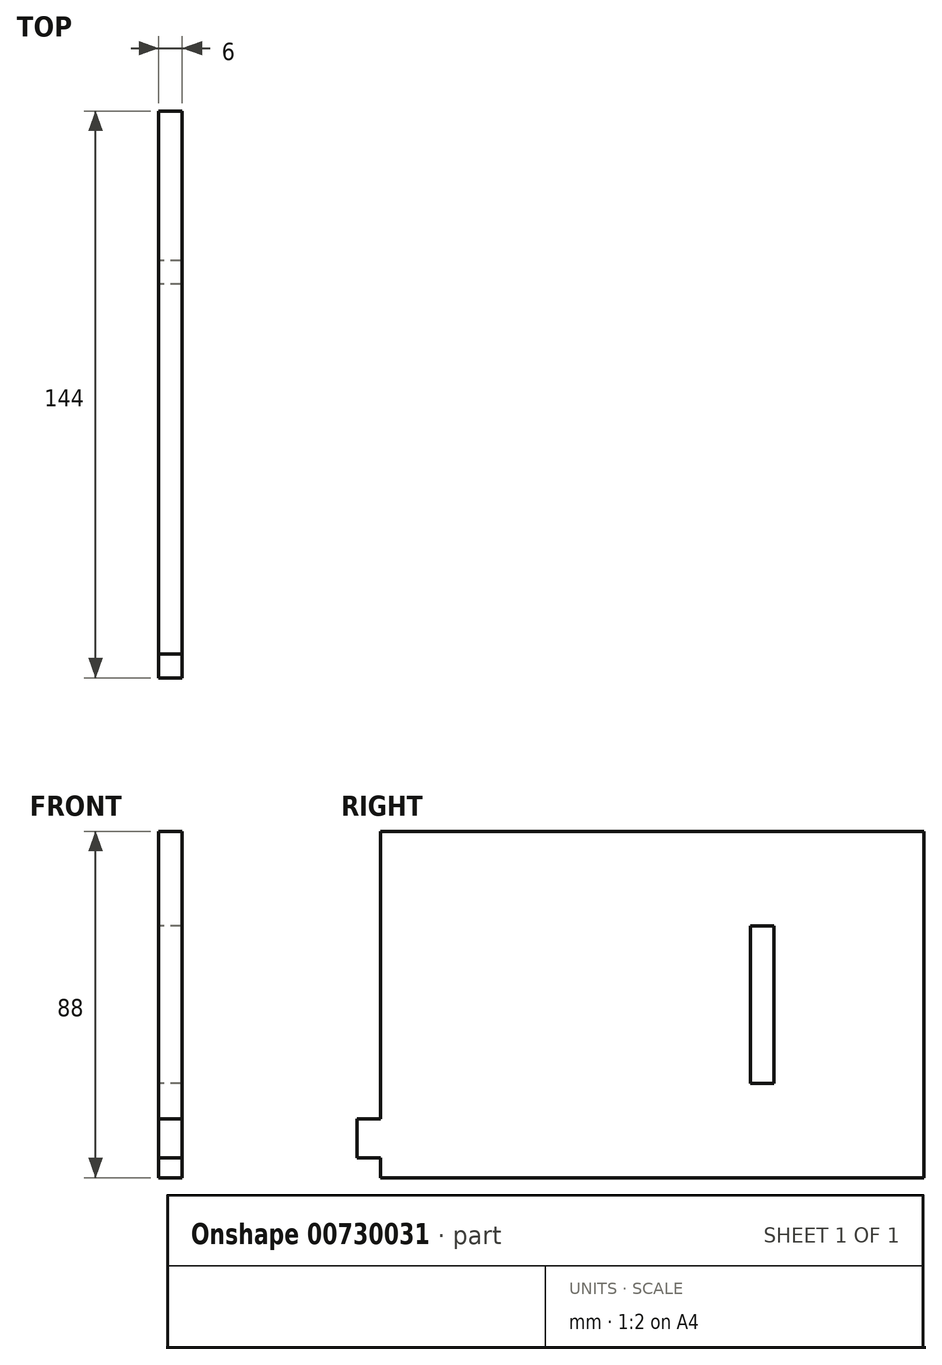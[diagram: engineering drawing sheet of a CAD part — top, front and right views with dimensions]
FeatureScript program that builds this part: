
annotation { "Feature Type Name" : "Feature", "Feature Type Description" : "" }
export const myFeature = defineFeature(function(context is Context, id is Id, definition is map)
    precondition{}
    {
        {
            var Q0;
            Q0=qCreatedBy(makeId("Right.planeOp"),FACE);
            var sketch = newSketch(context, id + "F0", { "sketchPlane" : qUnion([Q0])});
            skLineSegment(sketch, "E0", {"start": v(66.06, -36.03) * mm, "end": v(-71.94, -36.03) * mm});
            skLineSegment(sketch, "E1", {"start": v(-71.94, -36.03) * mm, "end": v(-71.94, -31.03) * mm});
            skLineSegment(sketch, "E2", {"start": v(-71.94, -31.03) * mm, "end": v(-77.94, -31.03) * mm});
            skLineSegment(sketch, "E3", {"start": v(-77.94, -31.03) * mm, "end": v(-77.94, -21.03) * mm});
            skLineSegment(sketch, "E4", {"start": v(-77.94, -21.03) * mm, "end": v(-71.94, -21.03) * mm});
            skLineSegment(sketch, "E5", {"start": v(-71.94, -21.03) * mm, "end": v(-71.94, 51.97) * mm});
            skLineSegment(sketch, "E6", {"start": v(-71.94, 51.97) * mm, "end": v(66.06, 51.97) * mm});
            skLineSegment(sketch, "E7", {"start": v(66.06, 51.97) * mm, "end": v(66.06, -36.03) * mm});
            skLineSegment(sketch, "E8", {"start": v(28.06, -12.03) * mm, "end": v(22.06, -12.03) * mm});
            skLineSegment(sketch, "E9", {"start": v(22.06, -12.03) * mm, "end": v(22.06, 27.97) * mm});
            skLineSegment(sketch, "E10", {"start": v(22.06, 27.97) * mm, "end": v(28.06, 27.97) * mm});
            skLineSegment(sketch, "E11", {"start": v(28.06, 27.97) * mm, "end": v(28.06, -12.03) * mm});
            skSolve(sketch);
        }
        {
            var Q0;
            Q0 = qSketchRegion(id + "F0", true);
            extrude(context, id + "F1", {"entities" : qUnion([Q0]), "depth" : 6 * mm, "offsetDistance" : 25 * mm});
        }
    });
